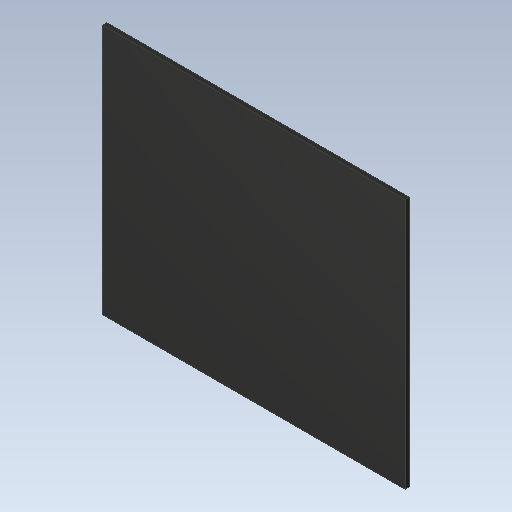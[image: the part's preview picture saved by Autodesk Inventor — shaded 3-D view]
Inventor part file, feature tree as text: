
AUTODESK INVENTOR PART (.ipt)
format: ipt  version: 2023 (Build 270158000, 158)  size: 92,672 bytes
history: imported  units: in
note: dims shown in document units (in); Inventor stores cm internally (conversion verified against a paired STEP export)
features: imported_body x1
ambient origin geometry x8: Origin, YZ Plane, XZ Plane, XY Plane, X Axis, Y Axis, Z Axis, Center Point
bodies: Solid1 (imported_parasolid), Body1 (imported_parasolid)
feature tree (1):
  imported_body  NMx_Import_Brep_tag  [imported B-rep: ~6 faces, bbox_mm=[7.35, 6.1, 0.1]]
